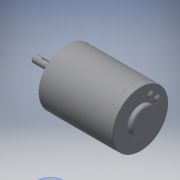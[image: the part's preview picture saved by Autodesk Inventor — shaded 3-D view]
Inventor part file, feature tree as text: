
AUTODESK INVENTOR PART (.ipt)
format: ipt  version: 2016 (Build 200138000, 138)  size: 166,912 bytes
history: native  units: in
note: dims shown in document units (in); Inventor stores cm internally (conversion verified against a paired STEP export)
features: chamfer x1
ambient origin geometry x8: Origin, YZ Plane, XZ Plane, XY Plane, X Axis, Y Axis, Z Axis, Center Point
bodies: Solid1 (feature_tree)
feature tree (1):
  chamfer  "Chamfer3"  [1 undecoded]
note: 1 required parameter value undecoded (feature->parameter linkage not recoverable at this tier; creation-order binding heuristic only, values carry confidence <= 0.55)
